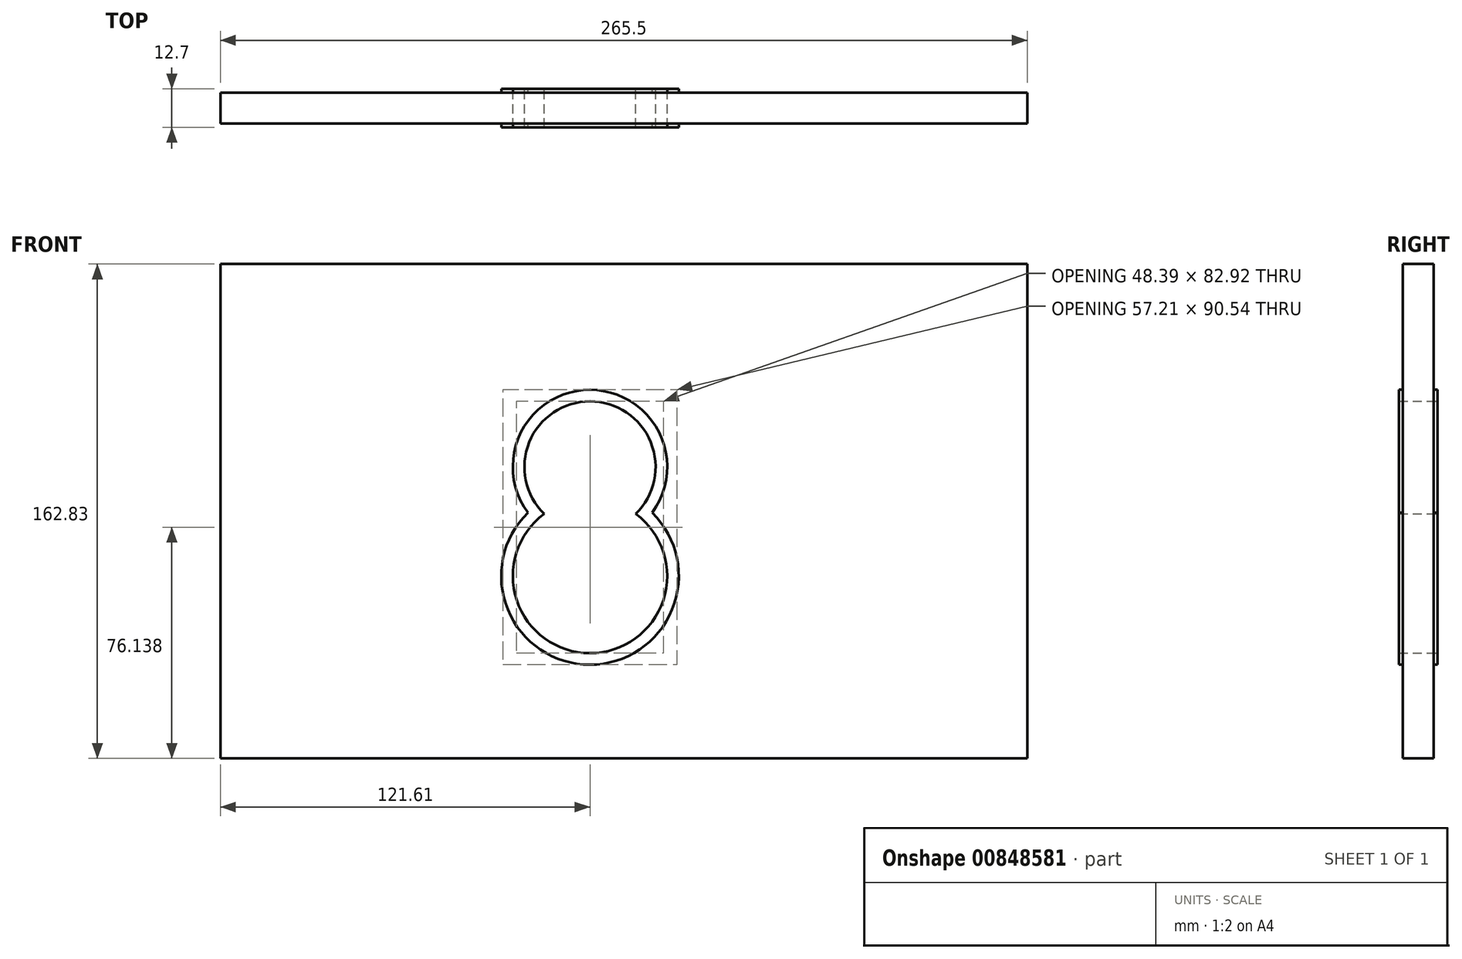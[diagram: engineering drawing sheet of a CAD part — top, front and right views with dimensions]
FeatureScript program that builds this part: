
annotation { "Feature Type Name" : "Feature", "Feature Type Description" : "" }
export const myFeature = defineFeature(function(context is Context, id is Id, definition is map)
    precondition{}
    {
        {
            var Q0;
            Q0=qCreatedBy(makeId("Front.planeOp"),FACE);
            var sketch = newSketch(context, id + "F0", { "sketchPlane" : qUnion([Q0])});
            skArc(sketch, "E0", {"start": v(-15.06, -1.8) * mm, "mid": v(0, -47.65) * mm, "end": v(15.06, -1.8) * mm});
            skArc(sketch, "E1", {"start": v(15.06, -1.8) * mm, "mid": v(0, 35.27) * mm, "end": v(-15.06, -1.8) * mm});
            skArc(sketch, "E2", {"start": v(20.45, -1.4) * mm, "mid": v(0, 39.08) * mm, "end": v(-20.45, -1.4) * mm});
            skArc(sketch, "E3", {"start": v(-20.45, -1.4) * mm, "mid": v(0, -51.46) * mm, "end": v(20.45, -1.4) * mm});
            skLineSegment(sketch, "E4.bottom", {"start": v(-121.61, 80.5) * mm, "end": v(143.9, 80.5) * mm});
            skLineSegment(sketch, "E4.top", {"start": v(-121.61, -82.33) * mm, "end": v(143.9, -82.33) * mm});
            skLineSegment(sketch, "E4.left", {"start": v(-121.61, 80.5) * mm, "end": v(-121.61, -82.33) * mm});
            skLineSegment(sketch, "E4.right", {"start": v(143.9, 80.5) * mm, "end": v(143.9, -82.33) * mm});
            skSolve(sketch);
        }
        {
            var Q0;
            Q0=makeQuery(id+"F0.imprint","IMPRINT",FACE,{"disambiguationData":[TD([[makeQuery(id+"F0.imprint","IMPRINT",EDGE,{"derivedFrom":sQuery(id+"F0.wireOp",EDGE,"E0")}),-1.0]])]});
            extrude(context, id + "F1", {"entities" : qUnion([Q0]), "endBound" : BoundingType.SYMMETRIC, "depth" : 12.7 * mm, "offsetDistance" : 25.4 * mm});
        }
        {
            var Q0;
            Q0 = qSketchRegion(id + "F0", true);
            extrude(context, id + "F2", {"entities" : qUnion([Q0]), "operationType" : NewBodyOperationType.ADD, "endBound" : BoundingType.SYMMETRIC, "depth" : 10.16 * mm, "offsetDistance" : 25.4 * mm});
        }
    });
